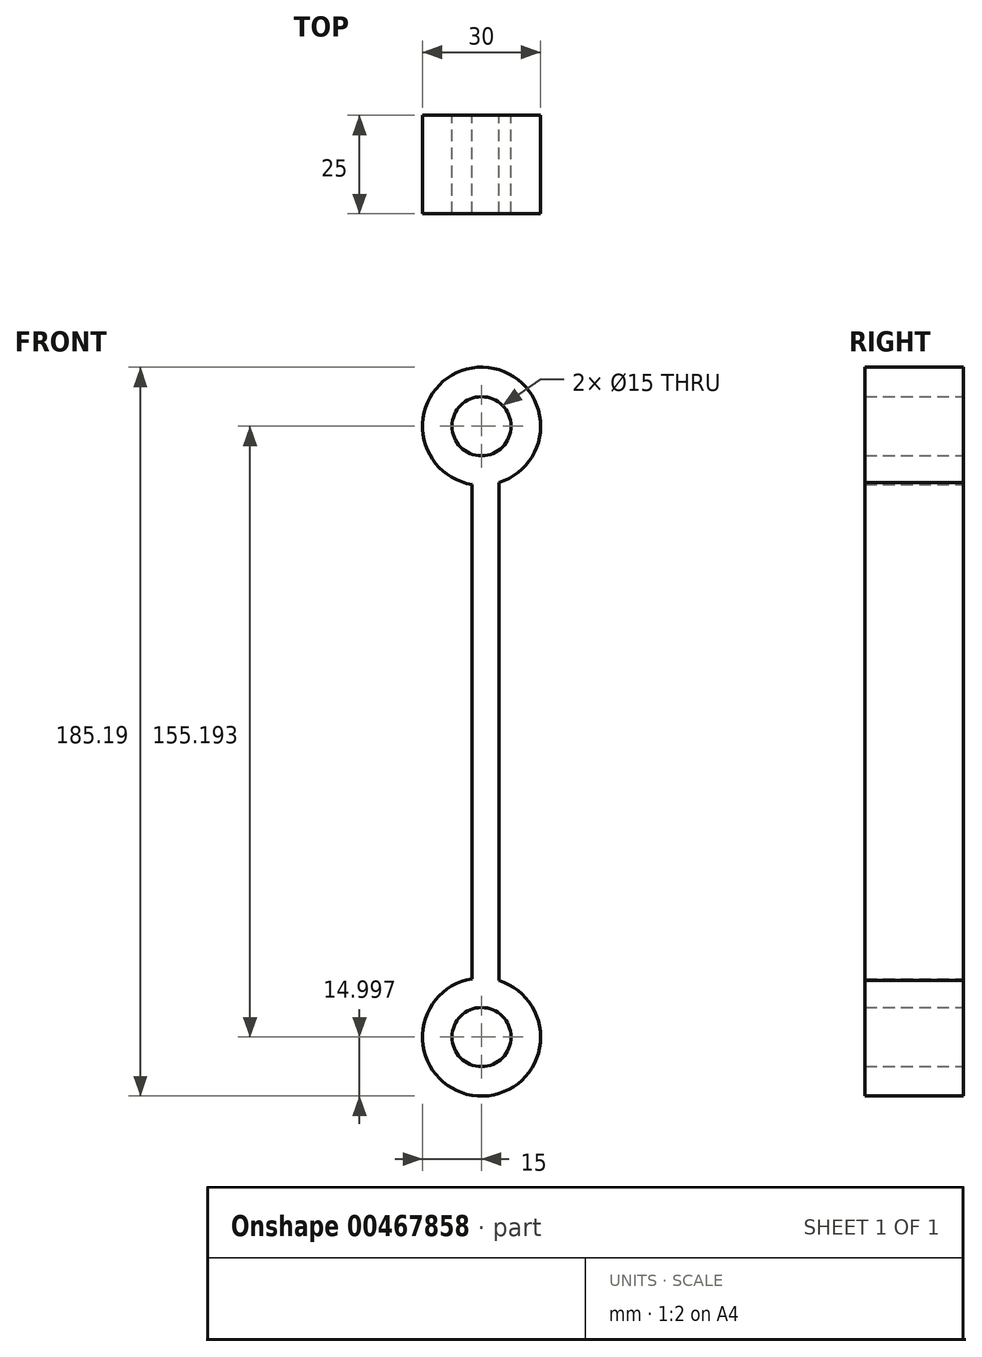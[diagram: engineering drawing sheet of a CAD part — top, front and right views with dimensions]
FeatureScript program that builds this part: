
annotation { "Feature Type Name" : "Feature", "Feature Type Description" : "" }
export const myFeature = defineFeature(function(context is Context, id is Id, definition is map)
    precondition{}
    {
        {
            var Q0;
            Q0=qCreatedBy(makeId("Front.planeOp"),FACE);
            var sketch = newSketch(context, id + "F0", { "sketchPlane" : qUnion([Q0])});
            skCircle(sketch, "E0", {"center": v(0, 0) * mm, "radius": 15 * mm});
            skCircle(sketch, "E1", {"center": v(0, 0) * mm, "radius": 7.5 * mm});
            skCircle(sketch, "E2", {"center": v(0, -155.2) * mm, "radius": 15 * mm});
            skCircle(sketch, "E3", {"center": v(0, -155.2) * mm, "radius": 7.5 * mm});
            skLineSegment(sketch, "E4", {"start": v(-2.4, -14.8) * mm, "end": v(-2.4, -170) * mm});
            skLineSegment(sketch, "E5", {"start": v(4.38, -14.35) * mm, "end": v(4.38, -140.85) * mm});
            skSolve(sketch);
        }
        {
            var Q0;
            Q0 = qSketchRegion(id + "F0", true);
            extrude(context, id + "F1", {"entities" : qUnion([Q0]), "depth" : 25 * mm});
        }
    });
